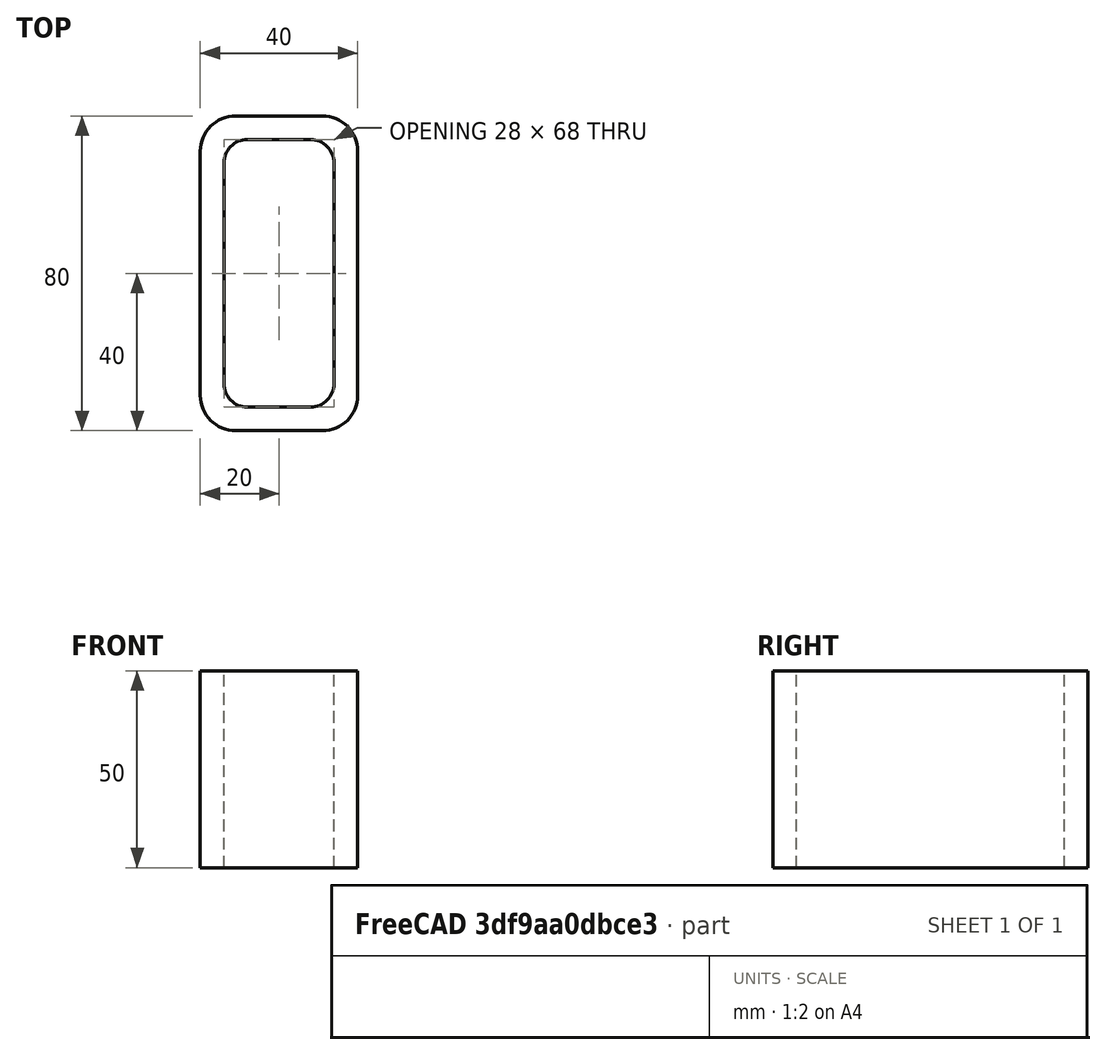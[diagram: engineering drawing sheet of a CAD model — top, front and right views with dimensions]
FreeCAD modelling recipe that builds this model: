
FCSTD DOCUMENT  (FreeCAD 0.15R4671 (Git))
Label: Rectangular hollow section 80x40x6 EN10219 S235JRH
License: All rights reserved
LicenseURL: http://en.wikipedia.org/wiki/All_rights_reserved
objects: Sketcher::SketchObject×1, Part::Extrusion×1
note: 2 computed .brp shape members not serialized (recipe doc carries the construction recipe); baked Part::Feature solids carry a one-line shape summary decoded from their .brp

FEATURE [Sketcher::SketchObject] Sketch
  sketch-geometry (16):
    g0: LineSegment StartX=-8 StartY=34 StartZ=0 EndX=8 EndY=34 EndZ=0
    g1: LineSegment StartX=14 StartY=28 StartZ=0 EndX=14 EndY=-28 EndZ=0
    g2: LineSegment StartX=8 StartY=-34 StartZ=0 EndX=-8 EndY=-34 EndZ=0
    g3: LineSegment StartX=-14 StartY=-28 StartZ=0 EndX=-14 EndY=28 EndZ=0
    g4: LineSegment StartX=-11 StartY=40 StartZ=0 EndX=11 EndY=40 EndZ=0
    g5: LineSegment StartX=20 StartY=31 StartZ=0 EndX=20 EndY=-31 EndZ=0
    g6: LineSegment StartX=11 StartY=-40 StartZ=0 EndX=-11 EndY=-40 EndZ=0
    g7: LineSegment StartX=-20 StartY=-31 StartZ=0 EndX=-20 EndY=31 EndZ=0
    g8: ArcOfCircle CenterX=-8 CenterY=28 CenterZ=0 NormalX=0 NormalY=0 NormalZ=1 Radius=6 StartAngle=1.5708 EndAngle=3.14159
    g9: ArcOfCircle CenterX=8 CenterY=28 CenterZ=0 NormalX=0 NormalY=0 NormalZ=1 Radius=6 StartAngle=0 EndAngle=1.5708
    g10: ArcOfCircle CenterX=8 CenterY=-28 CenterZ=0 NormalX=0 NormalY=0 NormalZ=1 Radius=6 StartAngle=4.71239 EndAngle=6.28319
    g11: ArcOfCircle CenterX=-8 CenterY=-28 CenterZ=0 NormalX=0 NormalY=0 NormalZ=1 Radius=6 StartAngle=3.14159 EndAngle=4.71239
    g12: ArcOfCircle CenterX=11 CenterY=31 CenterZ=0 NormalX=0 NormalY=0 NormalZ=1 Radius=9 StartAngle=0 EndAngle=1.5708
    g13: ArcOfCircle CenterX=11 CenterY=-31 CenterZ=0 NormalX=0 NormalY=0 NormalZ=1 Radius=9 StartAngle=4.71239 EndAngle=6.28319
    g14: ArcOfCircle CenterX=-11 CenterY=-31 CenterZ=0 NormalX=0 NormalY=0 NormalZ=1 Radius=9 StartAngle=3.14159 EndAngle=4.71239
    g15: ArcOfCircle CenterX=-11 CenterY=31 CenterZ=0 NormalX=0 NormalY=0 NormalZ=1 Radius=9 StartAngle=1.5708 EndAngle=3.14159
  constraints (36):
    c: Horizontal(g2)
    c: Vertical(g3)
    c: Horizontal(g6)
    c: Vertical(g7)
    c: Tangent(g3,g8) = 1.5708
    c: Tangent(g0,g8) = 1.5708
    c: Tangent(g0,g9) = 1.5708
    c: Tangent(g1,g9) = 1.5708
    c: Tangent(g1,g10) = 1.5708
    c: Tangent(g2,g10) = 1.5708
    c: Tangent(g2,g11) = 1.5708
    c: Tangent(g3,g11) = 1.5708
    c: Tangent(g4,g12) = 1.5708
    c: Tangent(g5,g12) = 1.5708
    c: Tangent(g5,g13) = 1.5708
    c: Tangent(g6,g13) = 1.5708
    c: Tangent(g6,g14) = 1.5708
    c: Tangent(g7,g14) = 1.5708
    c: Tangent(g7,g15) = 1.5708
    c: Tangent(g4,g15) = 1.5708
    c: Equal(g9,g8)
    c: Equal(g9,g11)
    c: Equal(g9,g10)
    c: Equal(g12,g15)
    c: Equal(g12,g14)
    c: Equal(g12,g13)
    c: Symmetric(g4,g6,g-1)
    c: Symmetric(g7,g5,g-2)
    c: DistanceY(g4,g6) = -80
    c: DistanceX(g7,g5) = 40
    c: Symmetric(g3,g1,g-2)
    c: Symmetric(g0,g2,g-1)
    c: DistanceY(g0,g4) = 6
    c: DistanceX(g5,g1) = -6
    c: Radius(g9) = 6
    c: Radius(g12) = 9
FEATURE [Part::Extrusion] Extrude  label="Rectangular hollow section 80x40x6 EN10219 S235JRH"
  Base = -> Sketch
  Dir = (0,0,50)
  Solid = true
